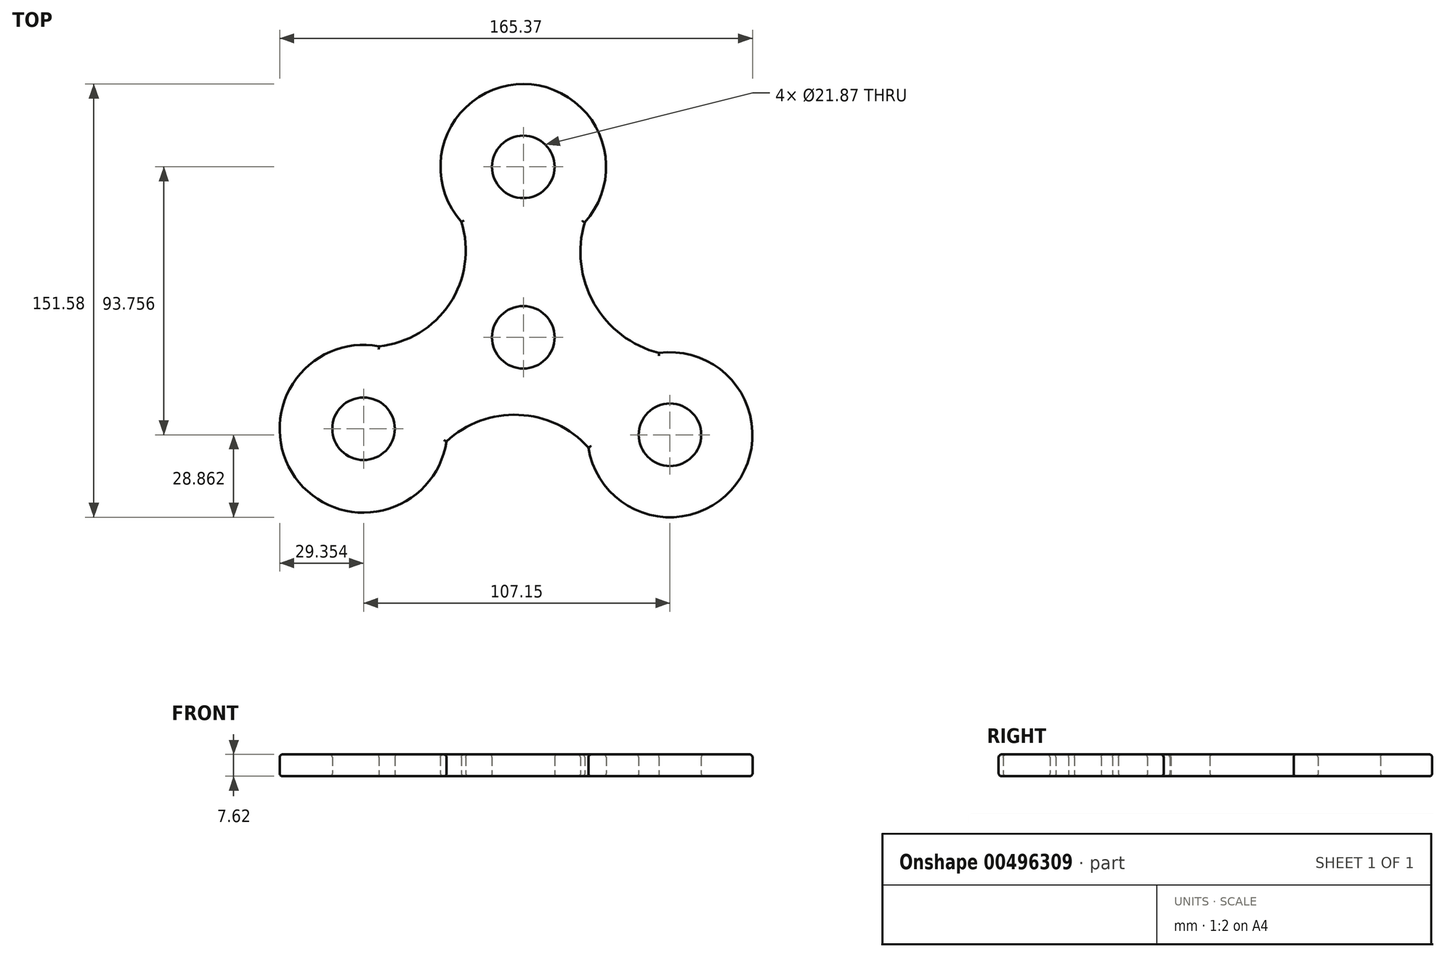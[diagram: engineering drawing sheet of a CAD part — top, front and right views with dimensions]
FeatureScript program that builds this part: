
annotation { "Feature Type Name" : "Feature", "Feature Type Description" : "" }
export const myFeature = defineFeature(function(context is Context, id is Id, definition is map)
    precondition{}
    {
        {
            var Q0;
            Q0=qCreatedBy(makeId("Top.planeOp"),FACE);
            var sketch = newSketch(context, id + "F0", { "sketchPlane" : qUnion([Q0])});
            skCircle(sketch, "E0", {"center": v(0, 49.7) * mm, "radius": 10.94 * mm});
            skCircle(sketch, "E1", {"center": v(-55.87, -41.94) * mm, "radius": 10.94 * mm});
            skCircle(sketch, "E2", {"center": v(0, -9.96) * mm, "radius": 10.94 * mm});
            skArc(sketch, "E3", {"start": v(-21.63, 30.43) * mm, "mid": v(0.1, 78.66) * mm, "end": v(21.48, 30.27) * mm});
            skArc(sketch, "E4", {"start": v(-50.51, -13.08) * mm, "mid": v(-79.8, -58.94) * mm, "end": v(-26.85, -46.4) * mm});
            skArc(sketch, "E5", {"start": v(22.76, -48.5) * mm, "mid": v(74.4, -61.33) * mm, "end": v(47.45, -15.45) * mm});
            skArc(sketch, "E6", {"start": v(-50.51, -13.08) * mm, "mid": v(-25.73, 1.81) * mm, "end": v(-21.63, 30.43) * mm});
            skArc(sketch, "E7", {"start": v(21.48, 30.27) * mm, "mid": v(24.75, 1.89) * mm, "end": v(47.45, -15.45) * mm});
            skArc(sketch, "E8", {"start": v(22.76, -48.5) * mm, "mid": v(-1.6, -37.09) * mm, "end": v(-26.85, -46.4) * mm});
            skPoint(sketch, "E9.orphan", {"position": v(-28.93, -30.28) * mm});
            skPoint(sketch, "E10.orphan", {"position": v(-28.93, -48.5) * mm});
            skCircle(sketch, "E11", {"center": v(51.28, -44.06) * mm, "radius": 10.94 * mm});
            skSolve(sketch);
        }
        {
            var Q0;
            Q0 = qSketchRegion(id + "F0", true);
            extrude(context, id + "F1", {"entities" : qUnion([Q0]), "depth" : 7.62 * mm});
        }
        {
            var Q0;
            Q0=makeQuery(id+"F1.opExtrude","CAP_EDGE",EDGE,{"disambiguationData":[OSD([sQuery(id+"F0.wireOp",EDGE,"E6")])],"isStart":false});
            var Q1;
            Q1=makeQuery(id+"F1.opExtrude","CAP_EDGE",EDGE,{"disambiguationData":[OSD([sQuery(id+"F0.wireOp",EDGE,"E7")])],"isStart":true});
            var Q2;
            Q2=makeQuery(id+"F1.opExtrude","CAP_EDGE",EDGE,{"disambiguationData":[OSD([sQuery(id+"F0.wireOp",EDGE,"E7")])],"isStart":false});
            var Q3;
            Q3=makeQuery(id+"F1.opExtrude","CAP_FACE",FACE,{"disambiguationData":[OSD([sQuery(id+"F0.wireOp",EDGE,"E0"),sQuery(id+"F0.wireOp",EDGE,"E1"),sQuery(id+"F0.wireOp",EDGE,"E2"),sQuery(id+"F0.wireOp",EDGE,"E3"),sQuery(id+"F0.wireOp",EDGE,"E4"),sQuery(id+"F0.wireOp",EDGE,"E5"),sQuery(id+"F0.wireOp",EDGE,"E6"),sQuery(id+"F0.wireOp",EDGE,"E7"),sQuery(id+"F0.wireOp",EDGE,"E8"),sQuery(id+"F0.wireOp",EDGE,"E11")])],"isStart":false});
            var Q4;
            Q4=makeQuery(id+"F1.opExtrude","CAP_EDGE",EDGE,{"disambiguationData":[OSD([sQuery(id+"F0.wireOp",EDGE,"E4")])],"isStart":false});
            var Q5;
            Q5=makeQuery(id+"F1.opExtrude","CAP_EDGE",EDGE,{"disambiguationData":[OSD([sQuery(id+"F0.wireOp",EDGE,"E8")])],"isStart":false});
            var Q6;
            Q6=makeQuery(id+"F1.opExtrude","CAP_EDGE",EDGE,{"disambiguationData":[OSD([sQuery(id+"F0.wireOp",EDGE,"E5")])],"isStart":false});
            var Q7;
            Q7=makeQuery(id+"F1.opExtrude","CAP_EDGE",EDGE,{"disambiguationData":[OSD([sQuery(id+"F0.wireOp",EDGE,"E3")])],"isStart":false});
            fillet(context, id + "F2", {"entities" : qUnion([Q0, Q1, Q2, Q3, Q4, Q5, Q6, Q7]), "radius" : 1 * mm, "tangentPropagation" : true, "allowEdgeOverflow" : false});
        }
        {
            var Q0;
            Q0=makeQuery(id+"F1.opExtrude","CAP_FACE",FACE,{"disambiguationData":[OSD([sQuery(id+"F0.wireOp",EDGE,"E0"),sQuery(id+"F0.wireOp",EDGE,"E1"),sQuery(id+"F0.wireOp",EDGE,"E2"),sQuery(id+"F0.wireOp",EDGE,"E3"),sQuery(id+"F0.wireOp",EDGE,"E4"),sQuery(id+"F0.wireOp",EDGE,"E5"),sQuery(id+"F0.wireOp",EDGE,"E6"),sQuery(id+"F0.wireOp",EDGE,"E7"),sQuery(id+"F0.wireOp",EDGE,"E8"),sQuery(id+"F0.wireOp",EDGE,"E11")])],"isStart":true});
            fillet(context, id + "F3", {"entities" : qUnion([Q0]), "radius" : 1 * mm, "tangentPropagation" : true, "allowEdgeOverflow" : false});
        }
    });
